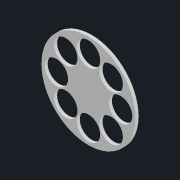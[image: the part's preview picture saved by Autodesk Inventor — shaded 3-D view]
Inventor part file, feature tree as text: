
AUTODESK INVENTOR PART (.ipt)
format: ipt  version: 2022.2 (Build 262287010, 287A)  size: 105,472 bytes
history: native  units: mm
features: extrude x1, sketch x1
ambient origin geometry x8: Origin, YZ Plane, XZ Plane, XY Plane, X Axis, Y Axis, Z Axis, Center Point
bodies: Solid1 (feature_tree)
feature tree (2):
  extrude  "Extrusion1"  Depth=20.5mm
  sketch  "Sketch1"  dims[d0=15.0mm d1=20.5mm d2=80.0mm d4=360.0deg d6=60.0mm d7=2.0mm d8=0.0mm]
